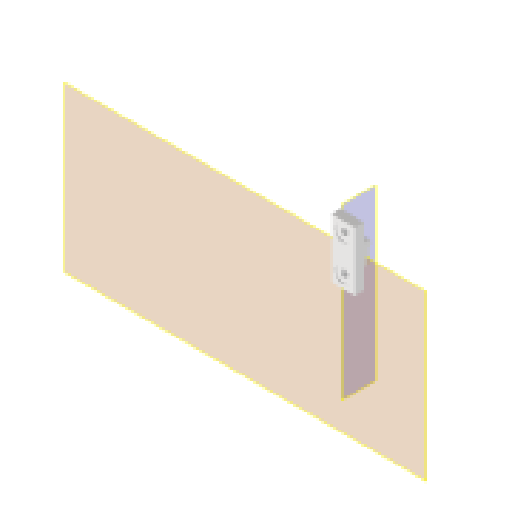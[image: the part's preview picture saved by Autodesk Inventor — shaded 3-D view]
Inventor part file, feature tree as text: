
AUTODESK INVENTOR PART (.ipt)
format: ipt  version: 2024.1 (Build 281209000, 209)  size: 123,904 bytes
history: native  units: mm
features: reference x3, plane x2, other x2, extrude x1, hole x1, fillet x1, sketch x1
ambient origin geometry x8: Origin, YZ Plane, XZ Plane, XY Plane, X Axis, Y Axis, Z Axis, Center Point
bodies: Volumenkörper1 (feature_tree)
feature tree (11):
  plane  "Arbeitsebene1"
  plane  "Arbeitsebene2"
  extrude  "Extrusion1"  Depth=1.0mm
  hole  "Bohrung1"  [1 undecoded]
  fillet  "Rundung1"  Radius=11.0mm
  sketch  "Skizze1"  dims[d0=8.0mm d1=1.0mm d2=3.5mm d3=11.0mm d4=9.0mm d5=0.0mm d6=2.8mm d7=6.0mm d8=6.5mm d9=0.5mm d10=90.0deg d11=8.0mm d12=20.594885mm d13=1.0mm d14=1.0mm]
  reference  "Referenz1"
  reference  "Referenz2"
  reference  "Referenz3"
  other  "Assembly_HoliSheet_v6.iam"
  other  "10_Wellplate_base_v6:1"
note: 1 required parameter value undecoded (feature->parameter linkage not recoverable at this tier; creation-order binding heuristic only, values carry confidence <= 0.55)
